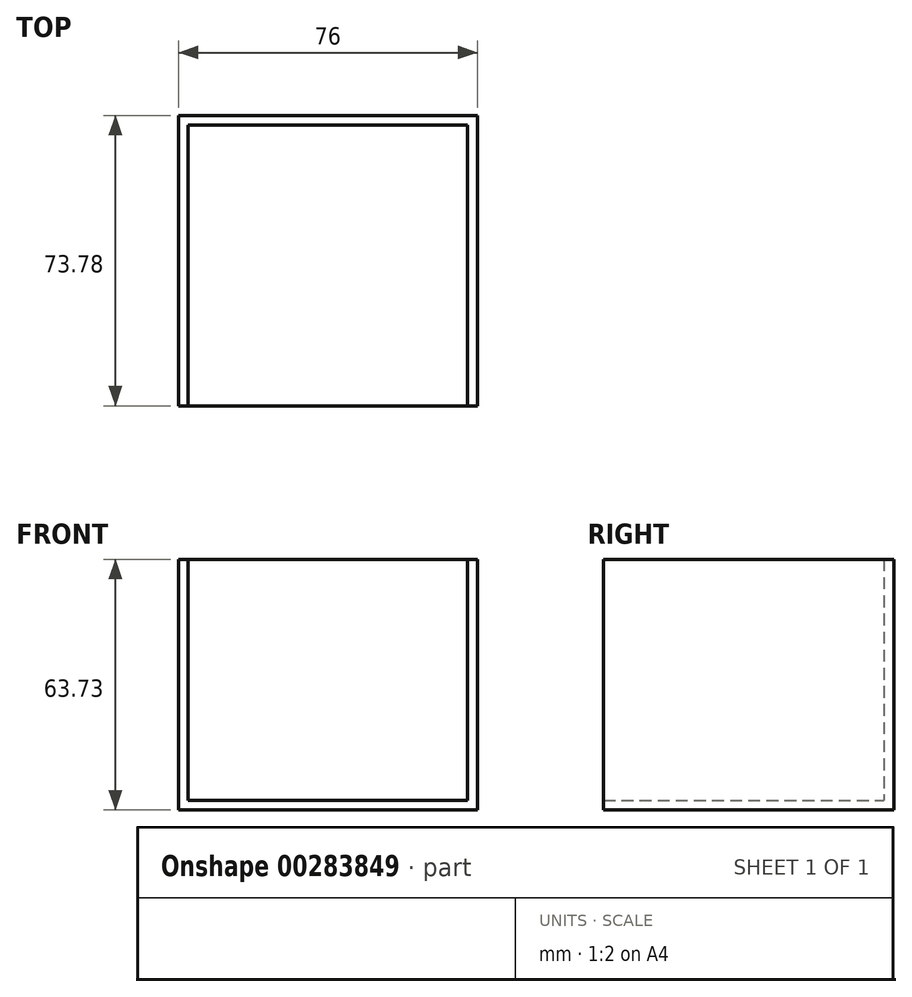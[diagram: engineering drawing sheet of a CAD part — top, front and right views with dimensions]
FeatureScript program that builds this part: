
annotation { "Feature Type Name" : "Feature", "Feature Type Description" : "" }
export const myFeature = defineFeature(function(context is Context, id is Id, definition is map)
    precondition{}
    {
        {
            var Q0;
            Q0=qCreatedBy(makeId("Front.planeOp"),FACE);
            var sketch = newSketch(context, id + "F0", { "sketchPlane" : qUnion([Q0])});
            skLineSegment(sketch, "E0.bottom", {"start": v(-36.67, 69.75) * mm, "end": v(39.33, 69.75) * mm});
            skLineSegment(sketch, "E0.top", {"start": v(-36.67, 6.02) * mm, "end": v(39.33, 6.02) * mm});
            skLineSegment(sketch, "E0.left", {"start": v(-36.67, 69.75) * mm, "end": v(-36.67, 6.02) * mm});
            skLineSegment(sketch, "E0.right", {"start": v(39.33, 69.75) * mm, "end": v(39.33, 6.02) * mm});
            skSolve(sketch);
        }
        {
            var Q0;
            Q0 = qSketchRegion(id + "F0", true);
            extrude(context, id + "F1", {"entities" : qUnion([Q0]), "depth" : 73.78 * mm});
        }
        {
            var Q0;
            Q0=makeQuery(id+"F1.opExtrude","CAP_FACE",FACE,{"disambiguationData":[OSD([sQuery(id+"F0.wireOp",EDGE,"E0.bottom"),sQuery(id+"F0.wireOp",EDGE,"E0.top"),sQuery(id+"F0.wireOp",EDGE,"E0.left"),sQuery(id+"F0.wireOp",EDGE,"E0.right")])],"isStart":false});
            var Q1;
            Q1=makeQuery(id+"F1.opExtrude","SWEPT_FACE",FACE,{"disambiguationData":[OSD([sQuery(id+"F0.wireOp",EDGE,"E0.bottom")])]});
            shell(context, id + "F2", {"entities" : qUnion([Q0, Q1]), "thickness" : 2.5 * mm});
        }
    });
